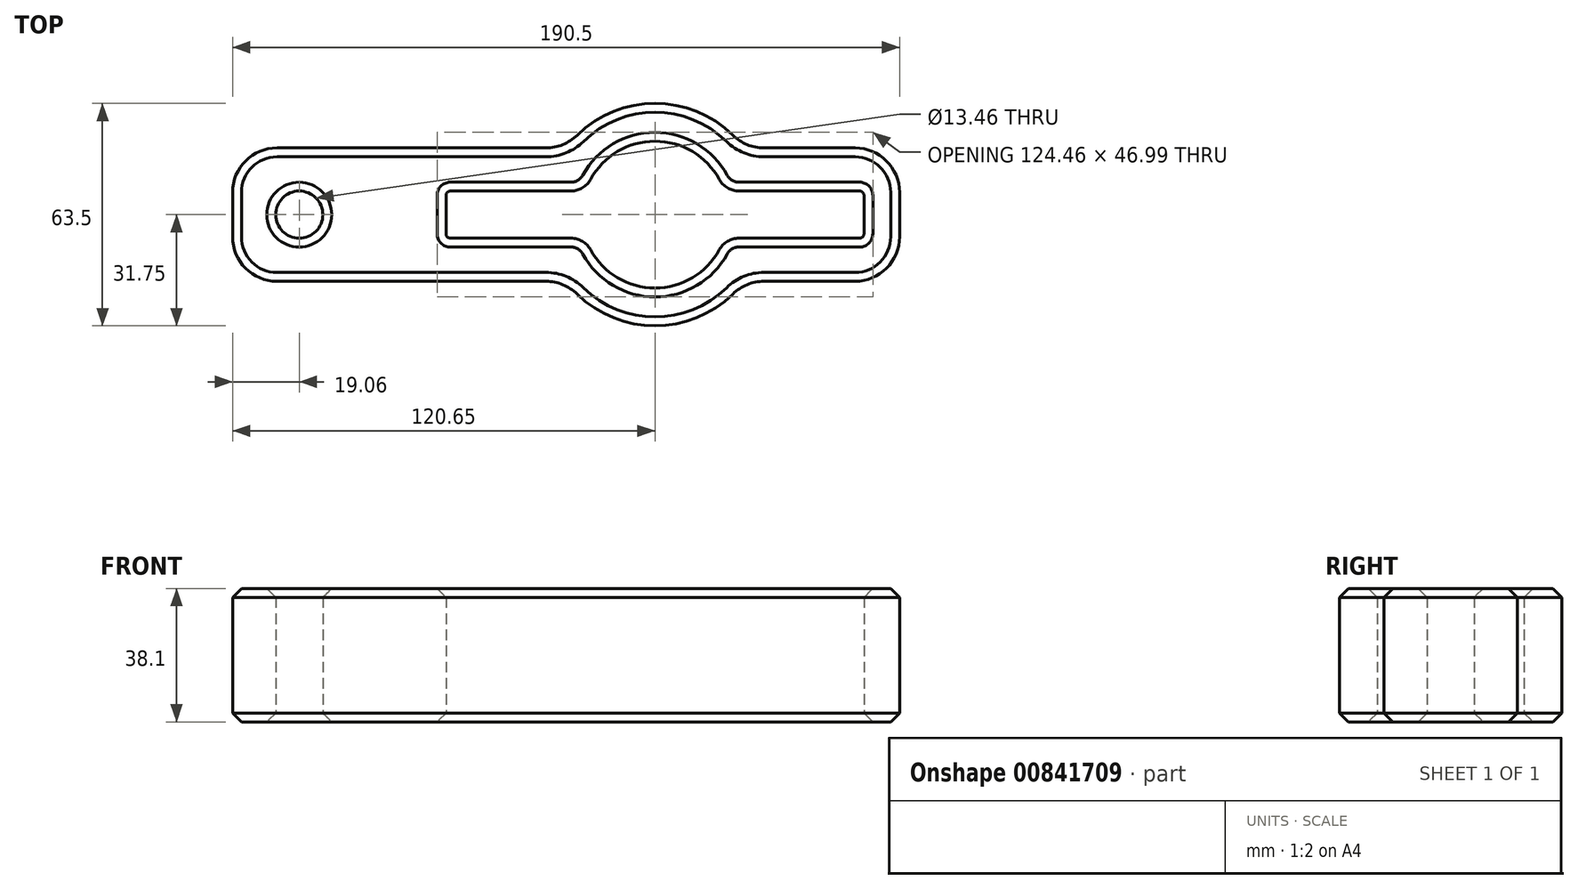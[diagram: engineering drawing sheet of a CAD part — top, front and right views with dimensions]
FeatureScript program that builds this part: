
annotation { "Feature Type Name" : "Feature", "Feature Type Description" : "" }
export const myFeature = defineFeature(function(context is Context, id is Id, definition is map)
    precondition{}
    {
        {
            var Q0;
            Q0=qCreatedBy(makeId("Top.planeOp"),FACE);
            var sketch = newSketch(context, id + "F0", { "sketchPlane" : qUnion([Q0])});
            skLineSegment(sketch, "E0.bottom", {"start": v(-69.85, 19.05) * mm, "end": v(69.85, 19.05) * mm});
            skLineSegment(sketch, "E0.top", {"start": v(-69.85, -19.05) * mm, "end": v(69.85, -19.05) * mm});
            skLineSegment(sketch, "E0.left", {"start": v(-69.85, 19.05) * mm, "end": v(-69.85, -19.05) * mm});
            skLineSegment(sketch, "E0.right", {"start": v(69.85, 19.05) * mm, "end": v(69.85, -19.05) * mm});
            skPoint(sketch, "E0.middle", {"position": v(0, 0) * mm});
            skSolve(sketch);
        }
        {
            var Q0;
            Q0 = qSketchRegion(id + "F0", true);
            extrude(context, id + "F1", {"entities" : qUnion([Q0]), "depth" : 38.1 * mm, "offsetDistance" : 25.4 * mm});
        }
        {
            var Q0;
            Q0=qCreatedBy(makeId("Top.planeOp"),FACE);
            var sketch = newSketch(context, id + "F2", { "sketchPlane" : qUnion([Q0])});
            skCircle(sketch, "E1", {"center": v(0, 0) * mm, "radius": 31.75 * mm});
            skSolve(sketch);
        }
        {
            var Q0;
            Q0 = qSketchRegion(id + "F2", true);
            var Q1;
            Q1=makeQuery(id+"F1.opExtrude","CAP_FACE",FACE,{"disambiguationData":[OSD([sQuery(id+"F0.wireOp",EDGE,"E0.bottom"),sQuery(id+"F0.wireOp",EDGE,"E0.top"),sQuery(id+"F0.wireOp",EDGE,"E0.left"),sQuery(id+"F0.wireOp",EDGE,"E0.right")])],"isStart":false});
            extrude(context, id + "F3", {"entities" : qUnion([Q0]), "operationType" : NewBodyOperationType.ADD, "endBound" : BoundingType.UP_TO_SURFACE, "depth" : 25.4 * mm, "endBoundEntityFace" : qUnion([Q1]), "offsetDistance" : 25.4 * mm});
        }
        {
            var Q0;
            Q0=qCreatedBy(makeId("Top.planeOp"),FACE);
            var sketch = newSketch(context, id + "F4", { "sketchPlane" : qUnion([Q0])});
            skLineSegment(sketch, "E2.bottom", {"start": v(-59.7, 6.73) * mm, "end": v(59.7, 6.73) * mm});
            skLineSegment(sketch, "E2.top", {"start": v(-59.7, -6.73) * mm, "end": v(59.7, -6.73) * mm});
            skLineSegment(sketch, "E2.left", {"start": v(-59.7, 6.73) * mm, "end": v(-59.7, -6.73) * mm});
            skLineSegment(sketch, "E2.right", {"start": v(59.7, 6.73) * mm, "end": v(59.7, -6.73) * mm});
            skPoint(sketch, "E2.middle", {"position": v(0, 0) * mm});
            skSolve(sketch);
        }
        {
            var Q0;
            Q0 = qSketchRegion(id + "F4", true);
            extrude(context, id + "F5", {"entities" : qUnion([Q0]), "operationType" : NewBodyOperationType.REMOVE, "endBound" : BoundingType.THROUGH_ALL, "depth" : 25.4 * mm, "offsetDistance" : 25.4 * mm});
        }
        {
            var Q0;
            Q0=qCreatedBy(makeId("Top.planeOp"),FACE);
            var sketch = newSketch(context, id + "F6", { "sketchPlane" : qUnion([Q0])});
            skCircle(sketch, "E3", {"center": v(0, 0) * mm, "radius": 20.96 * mm});
            skSolve(sketch);
        }
        {
            var Q0;
            Q0 = qSketchRegion(id + "F6", true);
            extrude(context, id + "F7", {"entities" : qUnion([Q0]), "operationType" : NewBodyOperationType.REMOVE, "endBound" : BoundingType.THROUGH_ALL, "depth" : 25.4 * mm, "offsetDistance" : 25.4 * mm});
        }
        {
            var Q0;
            Q0=qCreatedBy(makeId("Top.planeOp"),FACE);
            var sketch = newSketch(context, id + "F8", { "sketchPlane" : qUnion([Q0])});
            skLineSegment(sketch, "E4.bottom", {"start": v(-69.85, 19.05) * mm, "end": v(-120.65, 19.05) * mm});
            skLineSegment(sketch, "E4.top", {"start": v(-69.85, -19.05) * mm, "end": v(-120.65, -19.05) * mm});
            skLineSegment(sketch, "E4.left", {"start": v(-69.85, 19.05) * mm, "end": v(-69.85, -19.05) * mm});
            skLineSegment(sketch, "E4.right", {"start": v(-120.65, 19.05) * mm, "end": v(-120.65, -19.05) * mm});
            skSolve(sketch);
        }
        {
            var Q0;
            Q0 = qSketchRegion(id + "F8", true);
            var Q1;
            {var subQ0=sQuery(id+"F0.wireOp",EDGE,"E0.right");var subQ1=sQuery(id+"F0.wireOp",EDGE,"E0.left");var subQ2=sQuery(id+"F0.wireOp",EDGE,"E0.top");var subQ3=sQuery(id+"F0.wireOp",EDGE,"E0.bottom");Q1=makeQuery(id+"F3.boolean.opBoolean","MERGE",FACE,{"derivedFrom":[makeQuery(id+"F1.opExtrude","CAP_FACE",FACE,{"disambiguationData":[OSD([subQ3,subQ2,subQ1,subQ0])],"isStart":false}),makeQuery(id+"F3.opExtrude","CAP_FACE",FACE,{"disambiguationData":[OSD([subQ3,subQ2,subQ1,subQ0])],"isStart":false})]});}
            extrude(context, id + "F9", {"entities" : qUnion([Q0]), "operationType" : NewBodyOperationType.ADD, "endBound" : BoundingType.UP_TO_SURFACE, "depth" : 25.4 * mm, "endBoundEntityFace" : qUnion([Q1]), "offsetDistance" : 25.4 * mm});
        }
        {
            var Q0;
            Q0=makeQuery(id+"F3.boolean.opBoolean","INTERSECT",EDGE,{"disambiguationData":[OD(1.0)],"derivedFrom":[makeQuery(id+"F1.opExtrude","SWEPT_FACE",FACE,{"disambiguationData":[OSD([sQuery(id+"F0.wireOp",EDGE,"E0.top")])]}),makeQuery(id+"F3.opExtrude","SWEPT_FACE",FACE,{"disambiguationData":[OSD([sQuery(id+"F2.wireOp",EDGE,"E1")])]})]});
            var Q1;
            Q1=makeQuery(id+"F3.boolean.opBoolean","INTERSECT",EDGE,{"disambiguationData":[OD(0.0)],"derivedFrom":[makeQuery(id+"F1.opExtrude","SWEPT_FACE",FACE,{"disambiguationData":[OSD([sQuery(id+"F0.wireOp",EDGE,"E0.top")])]}),makeQuery(id+"F3.opExtrude","SWEPT_FACE",FACE,{"disambiguationData":[OSD([sQuery(id+"F2.wireOp",EDGE,"E1")])]})]});
            var Q2;
            Q2=makeQuery(id+"F3.boolean.opBoolean","INTERSECT",EDGE,{"disambiguationData":[OD(1.0)],"derivedFrom":[makeQuery(id+"F1.opExtrude","SWEPT_FACE",FACE,{"disambiguationData":[OSD([sQuery(id+"F0.wireOp",EDGE,"E0.bottom")])]}),makeQuery(id+"F3.opExtrude","SWEPT_FACE",FACE,{"disambiguationData":[OSD([sQuery(id+"F2.wireOp",EDGE,"E1")])]})]});
            var Q3;
            Q3=makeQuery(id+"F3.boolean.opBoolean","INTERSECT",EDGE,{"disambiguationData":[OD(0.0)],"derivedFrom":[makeQuery(id+"F1.opExtrude","SWEPT_FACE",FACE,{"disambiguationData":[OSD([sQuery(id+"F0.wireOp",EDGE,"E0.bottom")])]}),makeQuery(id+"F3.opExtrude","SWEPT_FACE",FACE,{"disambiguationData":[OSD([sQuery(id+"F2.wireOp",EDGE,"E1")])]})]});
            fillet(context, id + "F10", {"entities" : qUnion([Q0, Q1, Q2, Q3]), "radius" : 12.7 * mm, "tangentPropagation" : true, "allowEdgeOverflow" : false});
        }
        {
            var Q0;
            Q0=makeQuery(id+"F7.boolean.opBoolean","INTERSECT",EDGE,{"disambiguationData":[OD(1.0)],"derivedFrom":[makeQuery(id+"F5.boolean.opBoolean","COPY",FACE,{"derivedFrom":makeQuery(id+"F5.opExtrude","SWEPT_FACE",FACE,{"disambiguationData":[OSD([sQuery(id+"F4.wireOp",EDGE,"E2.top")])]})}),makeQuery(id+"F7.opExtrude","SWEPT_FACE",FACE,{"disambiguationData":[OSD([sQuery(id+"F6.wireOp",EDGE,"E3")])]})]});
            var Q1;
            Q1=makeQuery(id+"F7.boolean.opBoolean","INTERSECT",EDGE,{"disambiguationData":[OD(0.0)],"derivedFrom":[makeQuery(id+"F5.boolean.opBoolean","COPY",FACE,{"derivedFrom":makeQuery(id+"F5.opExtrude","SWEPT_FACE",FACE,{"disambiguationData":[OSD([sQuery(id+"F4.wireOp",EDGE,"E2.top")])]})}),makeQuery(id+"F7.opExtrude","SWEPT_FACE",FACE,{"disambiguationData":[OSD([sQuery(id+"F6.wireOp",EDGE,"E3")])]})]});
            var Q2;
            Q2=makeQuery(id+"F7.boolean.opBoolean","INTERSECT",EDGE,{"disambiguationData":[OD(0.0)],"derivedFrom":[makeQuery(id+"F5.boolean.opBoolean","COPY",FACE,{"derivedFrom":makeQuery(id+"F5.opExtrude","SWEPT_FACE",FACE,{"disambiguationData":[OSD([sQuery(id+"F4.wireOp",EDGE,"E2.bottom")])]})}),makeQuery(id+"F7.opExtrude","SWEPT_FACE",FACE,{"disambiguationData":[OSD([sQuery(id+"F6.wireOp",EDGE,"E3")])]})]});
            var Q3;
            Q3=makeQuery(id+"F7.boolean.opBoolean","INTERSECT",EDGE,{"disambiguationData":[OD(1.0)],"derivedFrom":[makeQuery(id+"F5.boolean.opBoolean","COPY",FACE,{"derivedFrom":makeQuery(id+"F5.opExtrude","SWEPT_FACE",FACE,{"disambiguationData":[OSD([sQuery(id+"F4.wireOp",EDGE,"E2.bottom")])]})}),makeQuery(id+"F7.opExtrude","SWEPT_FACE",FACE,{"disambiguationData":[OSD([sQuery(id+"F6.wireOp",EDGE,"E3")])]})]});
            fillet(context, id + "F11", {"entities" : qUnion([Q0, Q1, Q2, Q3]), "radius" : 6.35 * mm, "tangentPropagation" : true, "allowEdgeOverflow" : false});
        }
        {
            var Q0;
            Q0=makeQuery(id+"F5.boolean.opBoolean","COPY",EDGE,{"derivedFrom":makeQuery(id+"F5.opExtrude","SWEPT_EDGE",EDGE,{"disambiguationData":[OSD([sQuery(id+"F4.wireOp",EDGE,"E2.bottom"),sQuery(id+"F4.wireOp",EDGE,"E2.right")])]})});
            var Q1;
            Q1=makeQuery(id+"F5.boolean.opBoolean","COPY",EDGE,{"derivedFrom":makeQuery(id+"F5.opExtrude","SWEPT_EDGE",EDGE,{"disambiguationData":[OSD([sQuery(id+"F4.wireOp",EDGE,"E2.bottom"),sQuery(id+"F4.wireOp",EDGE,"E2.left")])]})});
            var Q2;
            Q2=makeQuery(id+"F5.boolean.opBoolean","COPY",EDGE,{"derivedFrom":makeQuery(id+"F5.opExtrude","SWEPT_EDGE",EDGE,{"disambiguationData":[OSD([sQuery(id+"F4.wireOp",EDGE,"E2.top"),sQuery(id+"F4.wireOp",EDGE,"E2.left")])]})});
            var Q3;
            Q3=makeQuery(id+"F5.boolean.opBoolean","COPY",EDGE,{"derivedFrom":makeQuery(id+"F5.opExtrude","SWEPT_EDGE",EDGE,{"disambiguationData":[OSD([sQuery(id+"F4.wireOp",EDGE,"E2.top"),sQuery(id+"F4.wireOp",EDGE,"E2.right")])]})});
            fillet(context, id + "F12", {"entities" : qUnion([Q0, Q1, Q2, Q3]), "radius" : 1.27 * mm, "tangentPropagation" : true, "allowEdgeOverflow" : false});
        }
        {
            var Q0;
            Q0=makeQuery(id+"F1.opExtrude","SWEPT_EDGE",EDGE,{"disambiguationData":[OSD([sQuery(id+"F0.wireOp",EDGE,"E0.bottom"),sQuery(id+"F0.wireOp",EDGE,"E0.left")])]});
            var Q1;
            Q1=makeQuery(id+"F1.opExtrude","SWEPT_EDGE",EDGE,{"disambiguationData":[OSD([sQuery(id+"F0.wireOp",EDGE,"E0.top"),sQuery(id+"F0.wireOp",EDGE,"E0.left")])]});
            var Q2;
            Q2=makeQuery(id+"F1.opExtrude","SWEPT_EDGE",EDGE,{"disambiguationData":[OSD([sQuery(id+"F0.wireOp",EDGE,"E0.bottom"),sQuery(id+"F0.wireOp",EDGE,"E0.right")])]});
            var Q3;
            Q3=makeQuery(id+"F1.opExtrude","SWEPT_EDGE",EDGE,{"disambiguationData":[OSD([sQuery(id+"F0.wireOp",EDGE,"E0.top"),sQuery(id+"F0.wireOp",EDGE,"E0.right")])]});
            var Q4;
            Q4=makeQuery(id+"F9.opExtrude","SWEPT_EDGE",EDGE,{"disambiguationData":[OSD([sQuery(id+"F8.wireOp",EDGE,"E4.top"),sQuery(id+"F8.wireOp",EDGE,"E4.right")])]});
            var Q5;
            Q5=makeQuery(id+"F9.opExtrude","SWEPT_EDGE",EDGE,{"disambiguationData":[OSD([sQuery(id+"F8.wireOp",EDGE,"E4.bottom"),sQuery(id+"F8.wireOp",EDGE,"E4.right")])]});
            fillet(context, id + "F13", {"entities" : qUnion([Q0, Q1, Q2, Q3, Q4, Q5]), "radius" : 12.7 * mm, "tangentPropagation" : true, "allowEdgeOverflow" : false});
        }
        {
            var Q0;
            Q0=qCreatedBy(makeId("Top.planeOp"),FACE);
            var sketch = newSketch(context, id + "F14", { "sketchPlane" : qUnion([Q0])});
            skCircle(sketch, "E5", {"center": v(-101.59, 0) * mm, "radius": 6.73 * mm});
            skSolve(sketch);
        }
        {
            var Q0;
            Q0 = qSketchRegion(id + "F14", true);
            extrude(context, id + "F15", {"entities" : qUnion([Q0]), "operationType" : NewBodyOperationType.REMOVE, "endBound" : BoundingType.THROUGH_ALL, "depth" : 25.4 * mm, "offsetDistance" : 25.4 * mm});
        }
        {
            var Q0;
            {var subQ0=sQuery(id+"F0.wireOp",EDGE,"E0.right");var subQ1=sQuery(id+"F0.wireOp",EDGE,"E0.left");var subQ2=sQuery(id+"F0.wireOp",EDGE,"E0.top");var subQ3=sQuery(id+"F0.wireOp",EDGE,"E0.bottom");Q0=makeQuery(id+"F3.boolean.opBoolean","MERGE",FACE,{"derivedFrom":[makeQuery(id+"F1.opExtrude","CAP_FACE",FACE,{"disambiguationData":[OSD([subQ3,subQ2,subQ1,subQ0])],"isStart":false}),makeQuery(id+"F3.opExtrude","CAP_FACE",FACE,{"disambiguationData":[OSD([subQ3,subQ2,subQ1,subQ0])],"isStart":false})]});}
            var Q1;
            Q1=makeQuery(id+"F3.boolean.opBoolean","MERGE",FACE,{"derivedFrom":[makeQuery(id+"F1.opExtrude","CAP_FACE",FACE,{"disambiguationData":[OSD([sQuery(id+"F0.wireOp",EDGE,"E0.bottom"),sQuery(id+"F0.wireOp",EDGE,"E0.top"),sQuery(id+"F0.wireOp",EDGE,"E0.left"),sQuery(id+"F0.wireOp",EDGE,"E0.right")])],"isStart":true}),makeQuery(id+"F3.opExtrude","CAP_FACE",FACE,{"disambiguationData":[OSD([sQuery(id+"F2.wireOp",EDGE,"E1")])],"isStart":true})]});
            chamfer(context, id + "F16", {"entities" : qUnion([Q0, Q1]), "width" : 2.54 * mm, "tangentPropagation" : true});
        }
    });
